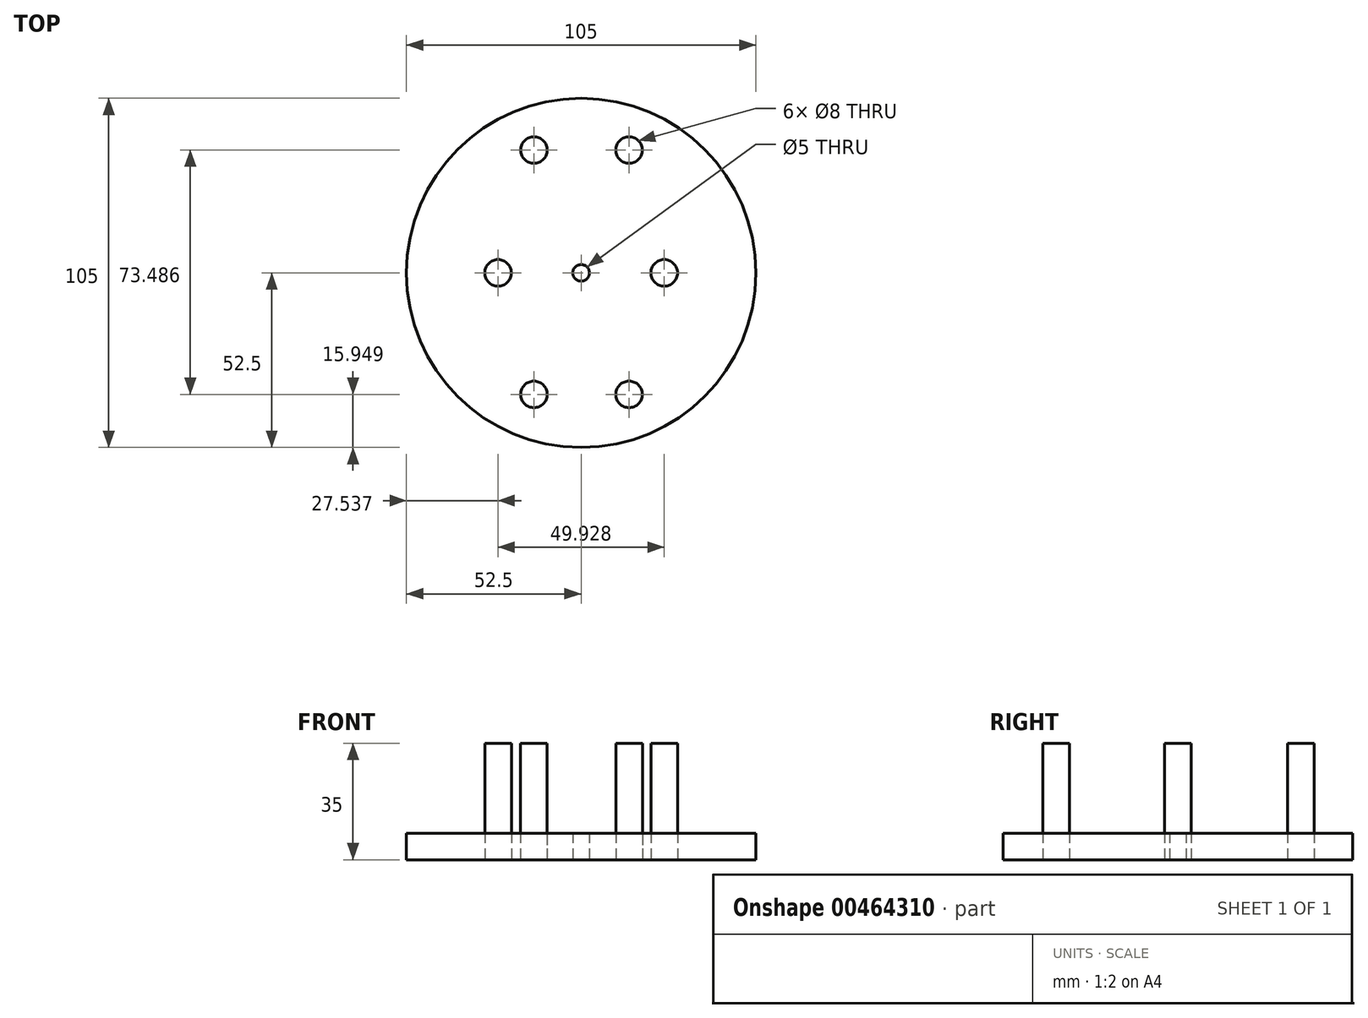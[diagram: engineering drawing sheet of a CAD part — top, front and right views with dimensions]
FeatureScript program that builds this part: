
annotation { "Feature Type Name" : "Feature", "Feature Type Description" : "" }
export const myFeature = defineFeature(function(context is Context, id is Id, definition is map)
    precondition{}
    {
        {
            var Q0;
            Q0=qCreatedBy(makeId("Top.planeOp"),FACE);
            var sketch = newSketch(context, id + "F0", { "sketchPlane" : qUnion([Q0])});
            skCircle(sketch, "E0", {"center": v(0, 0) * mm, "radius": 52.5 * mm});
            skPoint(sketch, "E1", {"position": v(-14.19, -36.55) * mm});
            skPoint(sketch, "E2", {"position": v(14.4, -36.55) * mm});
            skCircle(sketch, "E3", {"center": v(-14.19, -36.55) * mm, "radius": 4 * mm});
            skCircle(sketch, "E4", {"center": v(14.4, -36.55) * mm, "radius": 4 * mm});
            skPoint(sketch, "E5", {"position": v(-14.19, 36.94) * mm});
            skPoint(sketch, "E6", {"position": v(14.4, 36.94) * mm});
            skCircle(sketch, "E7", {"center": v(-14.19, 36.94) * mm, "radius": 4 * mm});
            skCircle(sketch, "E8", {"center": v(14.4, 36.94) * mm, "radius": 4 * mm});
            skPoint(sketch, "E9", {"position": v(24.96, 0) * mm});
            skPoint(sketch, "E10", {"position": v(-24.96, 0) * mm});
            skCircle(sketch, "E11", {"center": v(-24.96, 0) * mm, "radius": 4 * mm});
            skCircle(sketch, "E12", {"center": v(24.96, 0) * mm, "radius": 4 * mm});
            skCircle(sketch, "E13", {"center": v(0, 0) * mm, "radius": 2.5 * mm});
            skSolve(sketch);
        }
        {
            var Q0;
            Q0=makeQuery(id+"F0.imprint","IMPRINT",FACE,{"disambiguationData":[TD([[makeQuery(id+"F0.imprint","IMPRINT",EDGE,{"derivedFrom":sQuery(id+"F0.wireOp",EDGE,"E11")}),1.0]])]});
            var Q1;
            Q1=makeQuery(id+"F0.imprint","IMPRINT",FACE,{"disambiguationData":[TD([[makeQuery(id+"F0.imprint","IMPRINT",EDGE,{"derivedFrom":sQuery(id+"F0.wireOp",EDGE,"E3")}),1.0]])]});
            var Q2;
            Q2=makeQuery(id+"F0.imprint","IMPRINT",FACE,{"disambiguationData":[TD([[makeQuery(id+"F0.imprint","IMPRINT",EDGE,{"derivedFrom":sQuery(id+"F0.wireOp",EDGE,"E4")}),1.0]])]});
            var Q3;
            Q3=makeQuery(id+"F0.imprint","IMPRINT",FACE,{"disambiguationData":[TD([[makeQuery(id+"F0.imprint","IMPRINT",EDGE,{"derivedFrom":sQuery(id+"F0.wireOp",EDGE,"E12")}),1.0]])]});
            var Q4;
            Q4=makeQuery(id+"F0.imprint","IMPRINT",FACE,{"disambiguationData":[TD([[makeQuery(id+"F0.imprint","IMPRINT",EDGE,{"derivedFrom":sQuery(id+"F0.wireOp",EDGE,"E8")}),1.0]])]});
            var Q5;
            Q5=makeQuery(id+"F0.imprint","IMPRINT",FACE,{"disambiguationData":[TD([[makeQuery(id+"F0.imprint","IMPRINT",EDGE,{"derivedFrom":sQuery(id+"F0.wireOp",EDGE,"E7")}),1.0]])]});
            var Q6;
            Q6=sQuery(id+"F0.wireOp",EDGE,"E11");
            var Q7;
            Q7=sQuery(id+"F0.wireOp",EDGE,"E7");
            var Q8;
            Q8=sQuery(id+"F0.wireOp",EDGE,"E8");
            var Q9;
            Q9=sQuery(id+"F0.wireOp",EDGE,"E12");
            var Q10;
            Q10=sQuery(id+"F0.wireOp",EDGE,"E4");
            var Q11;
            Q11=sQuery(id+"F0.wireOp",EDGE,"E3");
            extrude(context, id + "F1", {"entities" : qUnion([Q0, Q1, Q2, Q3, Q4, Q5]), "surfaceEntities" : qUnion([Q6, Q7, Q8, Q9, Q10, Q11]), "depth" : 35 * mm, "offsetDistance" : 25.4 * mm});
        }
        {
            var Q0;
            Q0 = qSketchRegion(id + "F0", true);
            extrude(context, id + "F2", {"entities" : qUnion([Q0]), "depth" : 8 * mm, "offsetDistance" : 25.4 * mm});
        }
    });
